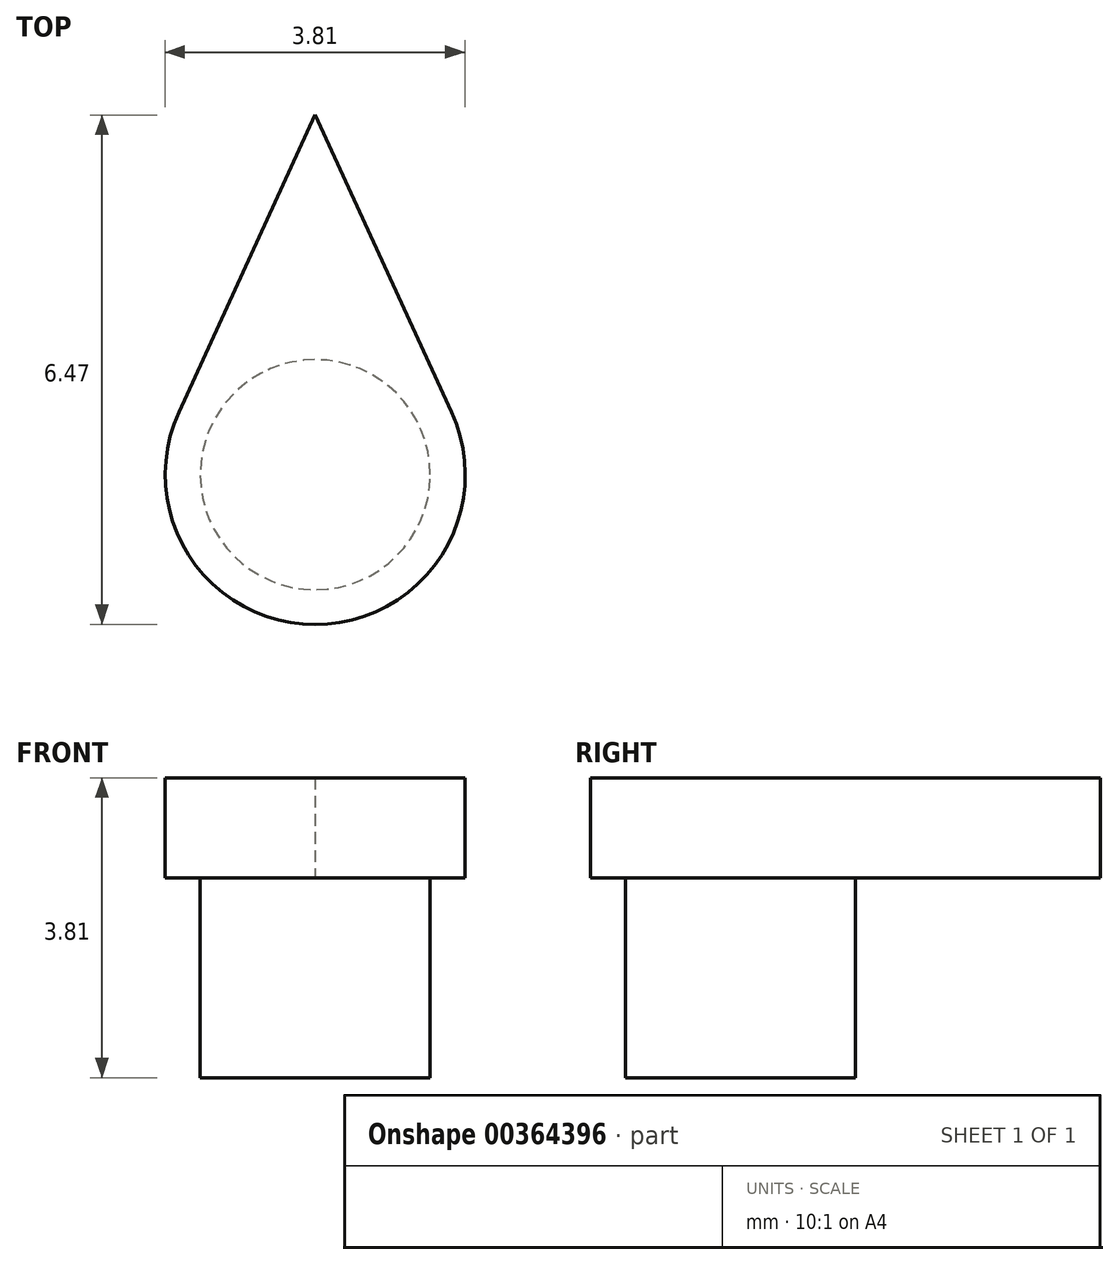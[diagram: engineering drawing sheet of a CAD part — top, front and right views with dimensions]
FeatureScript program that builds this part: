
annotation { "Feature Type Name" : "Feature", "Feature Type Description" : "" }
export const myFeature = defineFeature(function(context is Context, id is Id, definition is map)
    precondition{}
    {
        {
            var Q0;
            Q0=qCreatedBy(makeId("Top.planeOp"),FACE);
            var sketch = newSketch(context, id + "F0", { "sketchPlane" : qUnion([Q0])});
            skArc(sketch, "E0", {"start": v(-1.73, 0.8) * mm, "mid": v(0, -1.9) * mm, "end": v(1.73, 0.8) * mm});
            skLineSegment(sketch, "E1", {"start": v(-1.73, 0.8) * mm, "end": v(0, 4.57) * mm});
            skLineSegment(sketch, "E2", {"start": v(0, 4.57) * mm, "end": v(1.73, 0.8) * mm});
            skSolve(sketch);
        }
        {
            var Q0;
            Q0=makeQuery(id+"F0.imprint","IMPRINT",FACE,{"disambiguationData":[TD([[makeQuery(id+"F0.imprint","IMPRINT",EDGE,{"derivedFrom":sQuery(id+"F0.wireOp",EDGE,"E0")}),1.0]])]});
            extrude(context, id + "F1", {"entities" : qUnion([Q0]), "depth" : 1.27 * mm});
        }
        {
            var Q0;
            Q0=makeQuery(id+"F1.opExtrude","CAP_FACE",FACE,{"disambiguationData":[OSD([sQuery(id+"F0.wireOp",EDGE,"E0"),sQuery(id+"F0.wireOp",EDGE,"E1"),sQuery(id+"F0.wireOp",EDGE,"E2")])],"isStart":true});
            var sketch = newSketch(context, id + "F2", { "sketchPlane" : qUnion([Q0])});
            skCircle(sketch, "E3", {"center": v(0, 0) * mm, "radius": 1.46 * mm});
            skSolve(sketch);
        }
        {
            var Q0;
            Q0=makeQuery(id+"F2.imprint","IMPRINT",FACE,{"disambiguationData":[TD([[makeQuery(id+"F2.imprint","IMPRINT",EDGE,{"derivedFrom":sQuery(id+"F2.wireOp",EDGE,"E3")}),1.0]])]});
            extrude(context, id + "F3", {"entities" : qUnion([Q0]), "operationType" : NewBodyOperationType.ADD, "depth" : 2.54 * mm});
        }
    });
